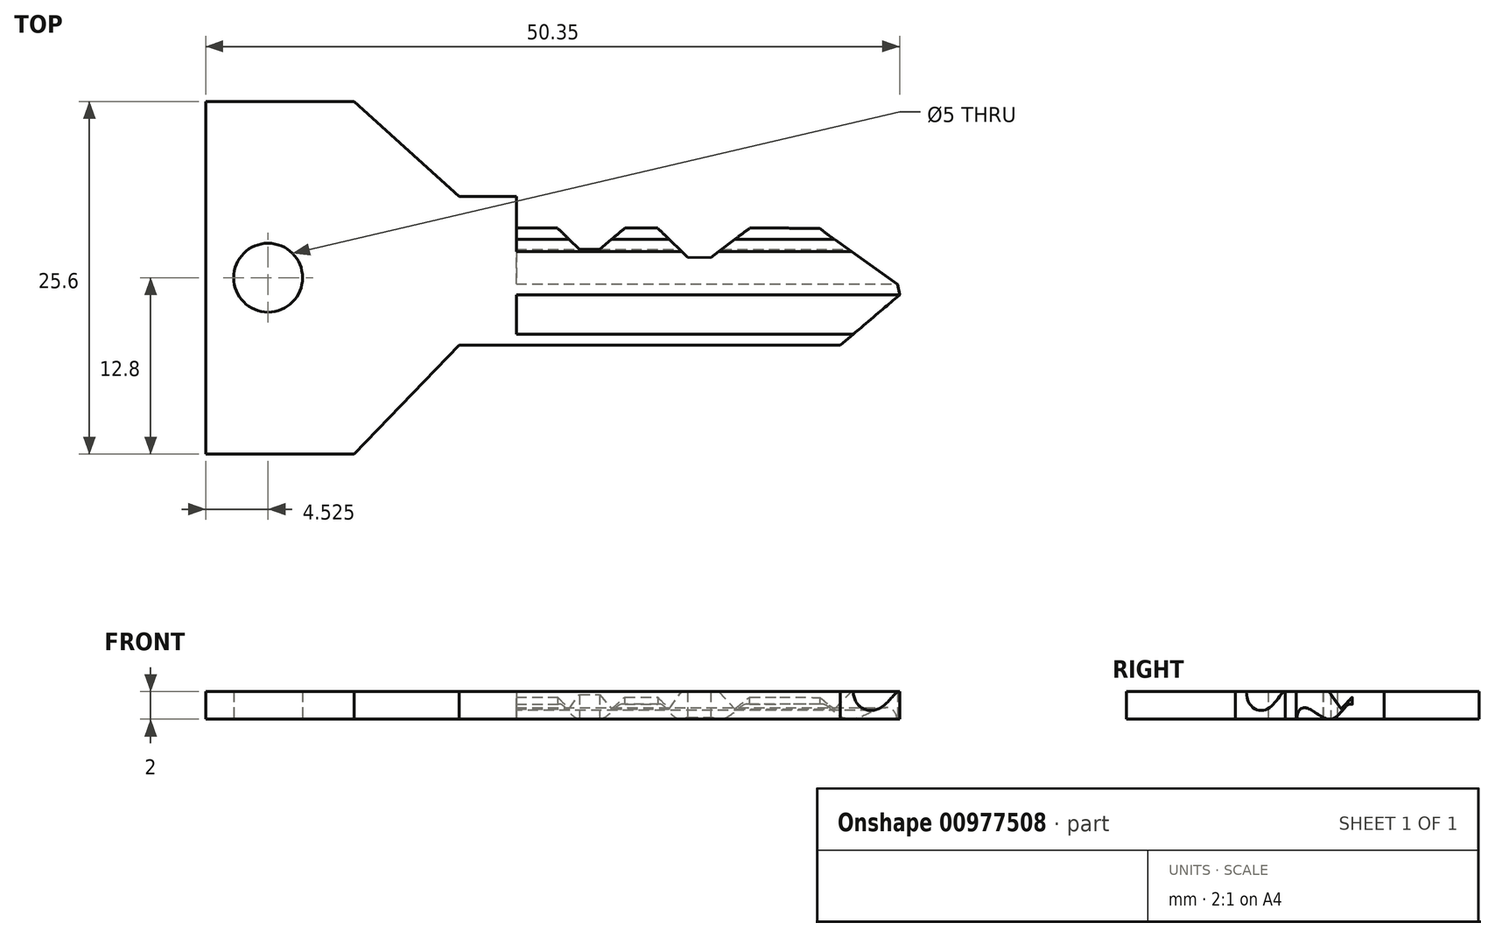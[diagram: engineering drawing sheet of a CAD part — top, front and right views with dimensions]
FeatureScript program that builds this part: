
annotation { "Feature Type Name" : "Feature", "Feature Type Description" : "" }
export const myFeature = defineFeature(function(context is Context, id is Id, definition is map)
    precondition{}
    {
        {
            var Q0;
            Q0=qCreatedBy(makeId("Top.planeOp"),FACE);
            var sketch = newSketch(context, id + "F0", { "sketchPlane" : qUnion([Q0])});
            skLineSegment(sketch, "E0", {"start": v(-19.92, 25.6) * mm, "end": v(-9.17, 25.6) * mm});
            skLineSegment(sketch, "E1", {"start": v(-9.17, 25.6) * mm, "end": v(-1.52, 25.6) * mm, "construction": true});
            skLineSegment(sketch, "E2", {"start": v(-9.17, 25.6) * mm, "end": v(-1.52, 18.7) * mm});
            skLineSegment(sketch, "E3", {"start": v(-1.52, 18.7) * mm, "end": v(2.62, 18.7) * mm});
            skLineSegment(sketch, "E4", {"start": v(2.62, 18.7) * mm, "end": v(2.62, 16.4) * mm});
            skLineSegment(sketch, "E5", {"start": v(2.62, 16.4) * mm, "end": v(30.52, 16.4) * mm});
            skLineSegment(sketch, "E6", {"start": v(30.52, 16.4) * mm, "end": v(30.52, 7.9) * mm});
            skLineSegment(sketch, "E7", {"start": v(30.52, 7.9) * mm, "end": v(-1.52, 7.9) * mm});
            skLineSegment(sketch, "E8", {"start": v(-1.52, 7.9) * mm, "end": v(-9.17, 0) * mm});
            skLineSegment(sketch, "E9", {"start": v(-9.17, 0) * mm, "end": v(-19.92, 0) * mm});
            skLineSegment(sketch, "E10", {"start": v(-22.9, 12.8) * mm, "end": v(30.52, 12.8) * mm, "construction": true});
            skCircle(sketch, "E11", {"center": v(-15.4, 12.8) * mm, "radius": 2.5 * mm});
            skLineSegment(sketch, "E12", {"start": v(-19.92, 25.6) * mm, "end": v(-19.92, 0) * mm});
            skSolve(sketch);
        }
        {
            var Q0;
            Q0=makeQuery(id+"F0.imprint","IMPRINT",FACE,{"disambiguationData":[TD([[makeQuery(id+"F0.imprint","IMPRINT",EDGE,{"derivedFrom":sQuery(id+"F0.wireOp",EDGE,"E0")}),-1.0]])]});
            extrude(context, id + "F1", {"entities" : qUnion([Q0]), "depth" : 2 * mm, "offsetDistance" : 25 * mm});
        }
        {
            var Q0;
            Q0=makeQuery(id+"F1.opExtrude","CAP_FACE",FACE,{"disambiguationData":[OSD([sQuery(id+"F0.wireOp",EDGE,"E0"),sQuery(id+"F0.wireOp",EDGE,"E2"),sQuery(id+"F0.wireOp",EDGE,"E3"),sQuery(id+"F0.wireOp",EDGE,"E4"),sQuery(id+"F0.wireOp",EDGE,"E5"),sQuery(id+"F0.wireOp",EDGE,"E6"),sQuery(id+"F0.wireOp",EDGE,"E7"),sQuery(id+"F0.wireOp",EDGE,"E8"),sQuery(id+"F0.wireOp",EDGE,"E9"),sQuery(id+"F0.wireOp",EDGE,"K2x9dN5n-Qaqd-zo9d-btnW-XQ1q8Ov544Ma"),sQuery(id+"F0.wireOp",EDGE,"E11")])],"isStart":false});
            var sketch = newSketch(context, id + "F2", { "sketchPlane" : qUnion([Q0])});
            skLineSegment(sketch, "E13", {"start": v(2.62, 18.7) * mm, "end": v(2.62, 15.15) * mm, "construction": true});
            skLineSegment(sketch, "E14", {"start": v(2.62, 15.15) * mm, "end": v(30.52, 15.15) * mm});
            skSolve(sketch);
        }
        {
            var Q0;
            Q0=makeQuery(id+"F1.opExtrude","SWEPT_FACE",FACE,{"disambiguationData":[OSD([sQuery(id+"F0.wireOp",EDGE,"E4")])]});
            var sketch = newSketch(context, id + "F3", { "sketchPlane" : qUnion([Q0])});
            skLineSegment(sketch, "E15", {"start": v(18.7, 2) * mm, "end": v(15.3, 2) * mm, "construction": true});
            skLineSegment(sketch, "E16", {"start": v(15.3, 2) * mm, "end": v(14.7, 2) * mm});
            skLineSegment(sketch, "E17", {"start": v(15.3, 2) * mm, "end": v(17.3, 2) * mm});
            skLineSegment(sketch, "E18", {"start": v(15.58, 0.75) * mm, "end": v(14.7, 2) * mm});
            skLineSegment(sketch, "E19", {"start": v(15.3, 2) * mm, "end": v(15.3, 0.75) * mm, "construction": true});
            skLineSegment(sketch, "E20", {"start": v(15.3, 0.75) * mm, "end": v(16.3, 0.75) * mm, "construction": true});
            skLineSegment(sketch, "E21", {"start": v(16.3, 0.75) * mm, "end": v(14.14, 0.75) * mm, "construction": true});
            skPoint(sketch, "E22.orphan", {"position": v(15.3, 1.15) * mm});
            skLineSegment(sketch, "E23", {"start": v(15.3, 0.75) * mm, "end": v(15.58, 0.75) * mm});
            skFitSpline(sketch, "E24", {"points": [v(15.58, 0.75) * mm, v(17.3, 2) * mm], "startDerivative": vector(3.04, 2.93) * mm, "endDerivative": vector(2.96, 0.82) * mm});
            skSolve(sketch);
        }
        {
            var Q0;
            Q0 = qSketchRegion(id + "F3", true);
            var Q1;
            Q1=sQuery(id+"F2.wireOp",EDGE,"E14");
            sweep(context, id + "F4", {"operationType" : NewBodyOperationType.REMOVE, "profiles" : qUnion([Q0]), "path" : qUnion([Q1])});
        }
        {
            var Q0;
            Q0=makeQuery(id+"F1.opExtrude","CAP_FACE",FACE,{"disambiguationData":[OSD([sQuery(id+"F0.wireOp",EDGE,"E0"),sQuery(id+"F0.wireOp",EDGE,"E2"),sQuery(id+"F0.wireOp",EDGE,"E3"),sQuery(id+"F0.wireOp",EDGE,"E4"),sQuery(id+"F0.wireOp",EDGE,"E5"),sQuery(id+"F0.wireOp",EDGE,"E6"),sQuery(id+"F0.wireOp",EDGE,"E7"),sQuery(id+"F0.wireOp",EDGE,"E8"),sQuery(id+"F0.wireOp",EDGE,"E9"),sQuery(id+"F0.wireOp",EDGE,"K2x9dN5n-Qaqd-zo9d-btnW-XQ1q8Ov544Ma"),sQuery(id+"F0.wireOp",EDGE,"E11")])],"isStart":false});
            var sketch = newSketch(context, id + "F5", { "sketchPlane" : qUnion([Q0])});
            skLineSegment(sketch, "E25", {"start": v(2.62, 18.7) * mm, "end": v(2.62, 10.25) * mm, "construction": true});
            skLineSegment(sketch, "E26", {"start": v(2.62, 10.25) * mm, "end": v(30.52, 10.25) * mm});
            skSolve(sketch);
        }
        {
            var Q0;
            Q0=makeQuery(id+"F4.boolean.opBoolean","MERGE",FACE,{"derivedFrom":[makeQuery(id+"F1.opExtrude","SWEPT_FACE",FACE,{"disambiguationData":[OSD([sQuery(id+"F0.wireOp",EDGE,"E4")])]})],"fromTools":[makeQuery(id+"F4.opSweep","CAP_FACE",FACE,{"disambiguationData":[OSD([sQuery(id+"F2.wireOp",VERTEX,"E14.start"),sQuery(id+"F3.wireOp",EDGE,"E16"),sQuery(id+"F3.wireOp",EDGE,"E17"),sQuery(id+"F3.wireOp",EDGE,"E18"),sQuery(id+"F3.wireOp",EDGE,"E24")])],"isStart":true})]});
            var sketch = newSketch(context, id + "F6", { "sketchPlane" : qUnion([Q0])});
            skPoint(sketch, "E27", {"position": v(10.25, 2) * mm});
            skLineSegment(sketch, "E28", {"start": v(10.25, 2) * mm, "end": v(10.25, 0.75) * mm, "construction": true});
            skLineSegment(sketch, "E29", {"start": v(10.32, 2) * mm, "end": v(10.25, 2) * mm, "construction": true});
            skLineSegment(sketch, "E30", {"start": v(10.25, 2) * mm, "end": v(11.55, 2) * mm, "construction": true});
            skLineSegment(sketch, "E31", {"start": v(10.25, 2) * mm, "end": v(8.7, 2) * mm, "construction": true});
            skFitSpline(sketch, "E32", {"points": [v(11.55, 2) * mm, v(10.25, 0.75) * mm, v(8.7, 2) * mm], "startDerivative": vector(-2.28, -0.4) * mm, "endDerivative": vector(-0.38, 7.3) * mm});
            skLineSegment(sketch, "E33", {"start": v(11.55, 2) * mm, "end": v(8.7, 2) * mm});
            skSolve(sketch);
        }
        {
            var Q0;
            Q0 = qSketchRegion(id + "F6", true);
            var Q1;
            Q1 = qConstructionFilter(qBodyType(qCreatedBy(id + "FOXifkE0uYtyl8m_1" ,EDGE), BodyType.WIRE), ConstructionObject.NO);
            var Q2;
            Q2=sQuery(id+"F5.wireOp",EDGE,"E26");
            sweep(context, id + "F7", {"operationType" : NewBodyOperationType.REMOVE, "profiles" : qUnion([Q0]), "surfaceProfiles" : qUnion([Q1]), "path" : qUnion([Q2])});
        }
        {
            var Q0;
            Q0=makeQuery(id+"F1.opExtrude","CAP_FACE",FACE,{"disambiguationData":[OSD([sQuery(id+"F0.wireOp",EDGE,"E0"),sQuery(id+"F0.wireOp",EDGE,"E2"),sQuery(id+"F0.wireOp",EDGE,"E3"),sQuery(id+"F0.wireOp",EDGE,"E4"),sQuery(id+"F0.wireOp",EDGE,"E5"),sQuery(id+"F0.wireOp",EDGE,"E6"),sQuery(id+"F0.wireOp",EDGE,"E7"),sQuery(id+"F0.wireOp",EDGE,"E8"),sQuery(id+"F0.wireOp",EDGE,"E9"),sQuery(id+"F0.wireOp",EDGE,"K2x9dN5n-Qaqd-zo9d-btnW-XQ1q8Ov544Ma"),sQuery(id+"F0.wireOp",EDGE,"E11")])],"isStart":true});
            var sketch = newSketch(context, id + "F8", { "sketchPlane" : qUnion([Q0])});
            skLineSegment(sketch, "E34", {"start": v(2.62, -18.7) * mm, "end": v(2.62, -17.2) * mm, "construction": true});
            skLineSegment(sketch, "E35", {"start": v(2.62, -17.2) * mm, "end": v(30.52, -17.2) * mm});
            skPoint(sketch, "E35.endSnap0", {"position": v(30.52, -12.15) * mm});
            skSolve(sketch);
        }
        {
            var Q0;
            Q0=makeQuery(id+"F4.boolean.opBoolean","MERGE",FACE,{"derivedFrom":[makeQuery(id+"F1.opExtrude","SWEPT_FACE",FACE,{"disambiguationData":[OSD([sQuery(id+"F0.wireOp",EDGE,"E4")])]})],"fromTools":[makeQuery(id+"F4.opSweep","CAP_FACE",FACE,{"disambiguationData":[OSD([sQuery(id+"F2.wireOp",VERTEX,"E14.start"),sQuery(id+"F3.wireOp",EDGE,"E16"),sQuery(id+"F3.wireOp",EDGE,"E17"),sQuery(id+"F3.wireOp",EDGE,"E18"),sQuery(id+"F3.wireOp",EDGE,"E24")])],"isStart":true})]});
            var sketch = newSketch(context, id + "F9", { "sketchPlane" : qUnion([Q0])});
            skPoint(sketch, "E36", {"position": v(18.7, 0) * mm});
            skLineSegment(sketch, "E37", {"start": v(18.7, 0) * mm, "end": v(17.2, 0) * mm});
            skLineSegment(sketch, "E38", {"start": v(17.2, 0) * mm, "end": v(14.85, 0) * mm, "construction": true});
            skLineSegment(sketch, "E39", {"start": v(17.2, 0) * mm, "end": v(17.2, 1) * mm, "construction": true});
            skLineSegment(sketch, "E40", {"start": v(18.7, 0) * mm, "end": v(13.1, 0) * mm, "construction": true});
            skLineSegment(sketch, "E41", {"start": v(13.1, 0) * mm, "end": v(13.1, 0.8) * mm, "construction": true});
            skLineSegment(sketch, "E42", {"start": v(13.1, 0) * mm, "end": v(12.35, 0) * mm, "construction": true});
            skFitSpline(sketch, "E43", {"points": [v(17.2, 1) * mm, v(16.02, 1) * mm, v(14.85, 0) * mm, v(13.1, 0.8) * mm, v(12.35, 0) * mm], "startDerivative": vector(-10.51, 0) * mm, "endDerivative": vector(-1.09, -9.32) * mm});
            skLineSegment(sketch, "E44", {"start": v(12.35, 0) * mm, "end": v(17.2, 0) * mm});
            skLineSegment(sketch, "E45", {"start": v(17.2, 0) * mm, "end": v(17.2, 1) * mm});
            skSolve(sketch);
        }
        {
            var Q0;
            Q0 = qSketchRegion(id + "F9", true);
            var Q1;
            Q1=sQuery(id+"F8.wireOp",EDGE,"E35");
            sweep(context, id + "F10", {"operationType" : NewBodyOperationType.REMOVE, "profiles" : qUnion([Q0]), "path" : qUnion([Q1])});
        }
        {
            var Q0;
            Q0=qCreatedBy(makeId("Top.planeOp"),FACE);
            var sketch = newSketch(context, id + "F11", { "sketchPlane" : qUnion([Q0])});
            skLineSegment(sketch, "E46", {"start": v(2.62, 18.7) * mm, "end": v(2.62, 16.7) * mm});
            skLineSegment(sketch, "E47", {"start": v(2.62, 16.7) * mm, "end": v(5.3, 16.7) * mm});
            skLineSegment(sketch, "E48", {"start": v(5.3, 16.7) * mm, "end": v(7.2, 14.84) * mm});
            skLineSegment(sketch, "E49", {"start": v(7.2, 14.84) * mm, "end": v(8.66, 14.84) * mm});
            skLineSegment(sketch, "E50", {"start": v(8.66, 14.84) * mm, "end": v(10.66, 16.55) * mm});
            skLineSegment(sketch, "E51", {"start": v(12.72, 16.55) * mm, "end": v(10.66, 16.55) * mm});
            skLineSegment(sketch, "E52", {"start": v(12.72, 16.55) * mm, "end": v(15.04, 14.3) * mm});
            skLineSegment(sketch, "E53", {"start": v(16.74, 14.27) * mm, "end": v(15.04, 14.3) * mm});
            skLineSegment(sketch, "E54", {"start": v(16.74, 14.27) * mm, "end": v(19.57, 16.41) * mm});
            skLineSegment(sketch, "E55", {"start": v(19.57, 16.41) * mm, "end": v(24.63, 16.38) * mm});
            skLineSegment(sketch, "E56", {"start": v(24.63, 16.38) * mm, "end": v(25.32, 15.85) * mm});
            skLineSegment(sketch, "E57", {"start": v(25.32, 15.85) * mm, "end": v(30.29, 12.33) * mm});
            skLineSegment(sketch, "E58", {"start": v(30.29, 12.33) * mm, "end": v(30.43, 11.54) * mm});
            skLineSegment(sketch, "E59", {"start": v(30.43, 11.54) * mm, "end": v(25.43, 7.33) * mm});
            skLineSegment(sketch, "E60", {"start": v(39.74, 11.25) * mm, "end": v(39.74, 18.7) * mm});
            skLineSegment(sketch, "E61", {"start": v(39.74, 18.7) * mm, "end": v(2.62, 18.7) * mm});
            skLineSegment(sketch, "E62", {"start": v(39.74, 7.56) * mm, "end": v(39.74, 18.7) * mm});
            skLineSegment(sketch, "E63", {"start": v(25.43, 7.33) * mm, "end": v(39.74, 7.56) * mm});
            skSolve(sketch);
        }
        {
            var Q0;
            Q0=makeQuery(id+"F11.imprint","IMPRINT",FACE,{"disambiguationData":[TD([[makeQuery(id+"F11.imprint","IMPRINT",EDGE,{"derivedFrom":sQuery(id+"F11.wireOp",EDGE,"E46")}),1.0]])]});
            extrude(context, id + "F12", {"entities" : qUnion([Q0]), "operationType" : NewBodyOperationType.REMOVE, "endBound" : BoundingType.THROUGH_ALL, "depth" : 25 * mm, "offsetDistance" : 25 * mm});
        }
    });
